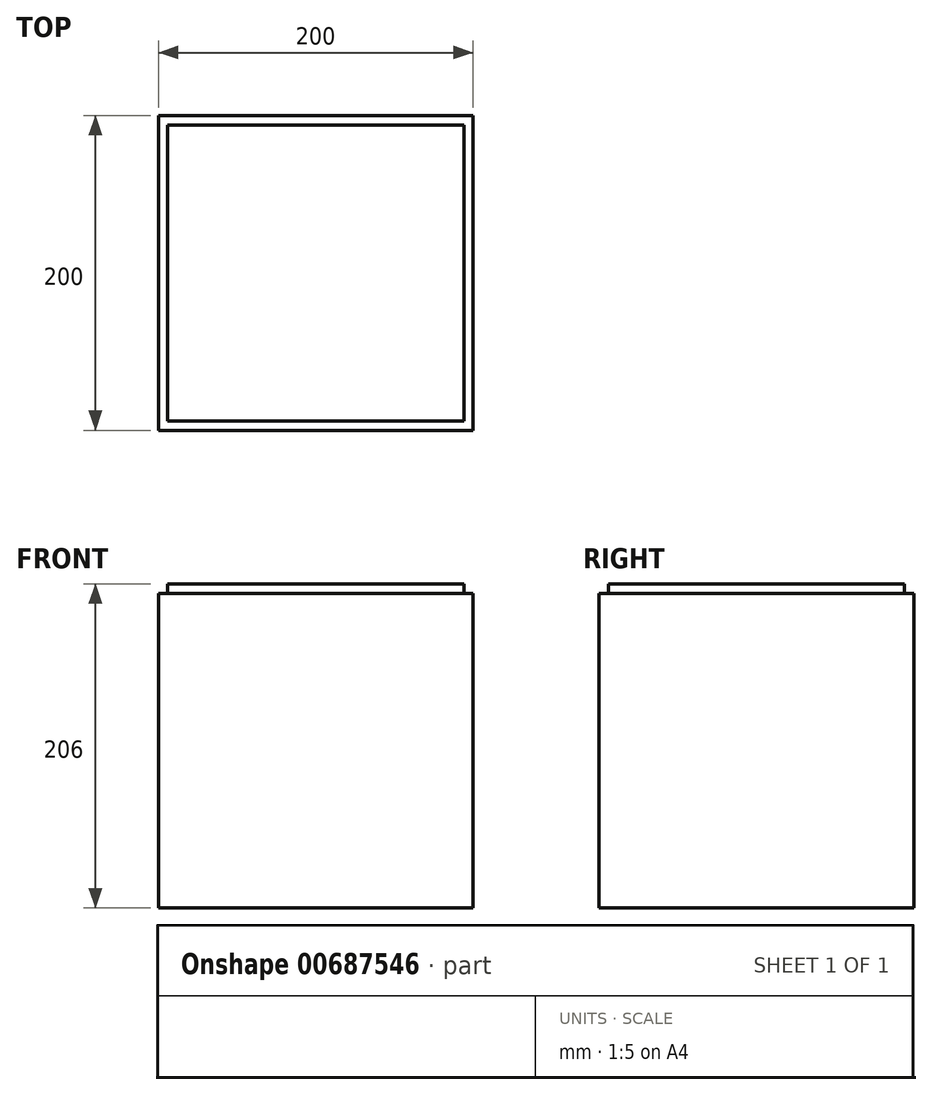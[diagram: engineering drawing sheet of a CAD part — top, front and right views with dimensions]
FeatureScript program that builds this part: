
annotation { "Feature Type Name" : "Feature", "Feature Type Description" : "" }
export const myFeature = defineFeature(function(context is Context, id is Id, definition is map)
    precondition{}
    {
        {
            var Q0;
            Q0=qCreatedBy(makeId("Front.planeOp"),FACE);
            var sketch = newSketch(context, id + "F0", { "sketchPlane" : qUnion([Q0])});
            skLineSegment(sketch, "E0.bottom", {"start": v(100, 100) * mm, "end": v(-100, 100) * mm});
            skLineSegment(sketch, "E0.top", {"start": v(100, -100) * mm, "end": v(-100, -100) * mm});
            skLineSegment(sketch, "E0.left", {"start": v(100, 100) * mm, "end": v(100, -100) * mm});
            skLineSegment(sketch, "E0.right", {"start": v(-100, 100) * mm, "end": v(-100, -100) * mm});
            skPoint(sketch, "E0.middle", {"position": v(0, 0) * mm});
            skSolve(sketch);
        }
        {
            var Q0;
            Q0=makeQuery(id+"F0.imprint","IMPRINT",FACE,{"disambiguationData":[TD([[makeQuery(id+"F0.imprint","IMPRINT",EDGE,{"derivedFrom":sQuery(id+"F0.wireOp",EDGE,"E0.bottom")}),1.0]])]});
            extrude(context, id + "F1", {"entities" : qUnion([Q0]), "endBound" : BoundingType.SYMMETRIC, "depth" : 200 * mm, "offsetDistance" : 25 * mm});
        }
        {
            var Q0;
            Q0=makeQuery(id+"F1.opExtrude","SWEPT_FACE",FACE,{"disambiguationData":[OSD([sQuery(id+"F0.wireOp",EDGE,"E0.bottom")])]});
            var sketch = newSketch(context, id + "F2", { "sketchPlane" : qUnion([Q0])});
            skLineSegment(sketch, "E1.bottom", {"start": v(94, 94) * mm, "end": v(-94, 94) * mm});
            skLineSegment(sketch, "E1.top", {"start": v(94, -94) * mm, "end": v(-94, -94) * mm});
            skLineSegment(sketch, "E1.left", {"start": v(94, 94) * mm, "end": v(94, -94) * mm});
            skLineSegment(sketch, "E1.right", {"start": v(-94, 94) * mm, "end": v(-94, -94) * mm});
            skPoint(sketch, "E1.middle", {"position": v(0, 0) * mm});
            skSolve(sketch);
        }
        {
            var Q0;
            Q0=makeQuery(id+"F2.imprint","IMPRINT",FACE,{"disambiguationData":[TD([[makeQuery(id+"F2.imprint","IMPRINT",EDGE,{"derivedFrom":sQuery(id+"F2.wireOp",EDGE,"E1.bottom")}),1.0]])]});
            extrude(context, id + "F3", {"entities" : qUnion([Q0]), "depth" : 6 * mm, "offsetDistance" : 25 * mm});
        }
    });
